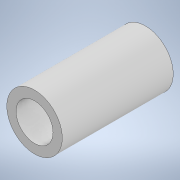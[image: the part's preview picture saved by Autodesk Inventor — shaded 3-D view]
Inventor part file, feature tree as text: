
AUTODESK INVENTOR PART (.ipt)
format: ipt  version: 2022 (Build 260153000, 153)  size: 95,744 bytes
history: native  units: mm
features: extrude x1, sketch x1
ambient origin geometry x8: Origin, YZ Plane, XZ Plane, XY Plane, X Axis, Y Axis, Z Axis, Center Point
bodies: Solid1 (feature_tree)
feature tree (2):
  extrude  "Extrusion1"  Depth=60.0mm
  sketch  "Sketch1"  dims[d0=20.0mm d1=30.0mm d2=60.0mm d3=0.0mm]
